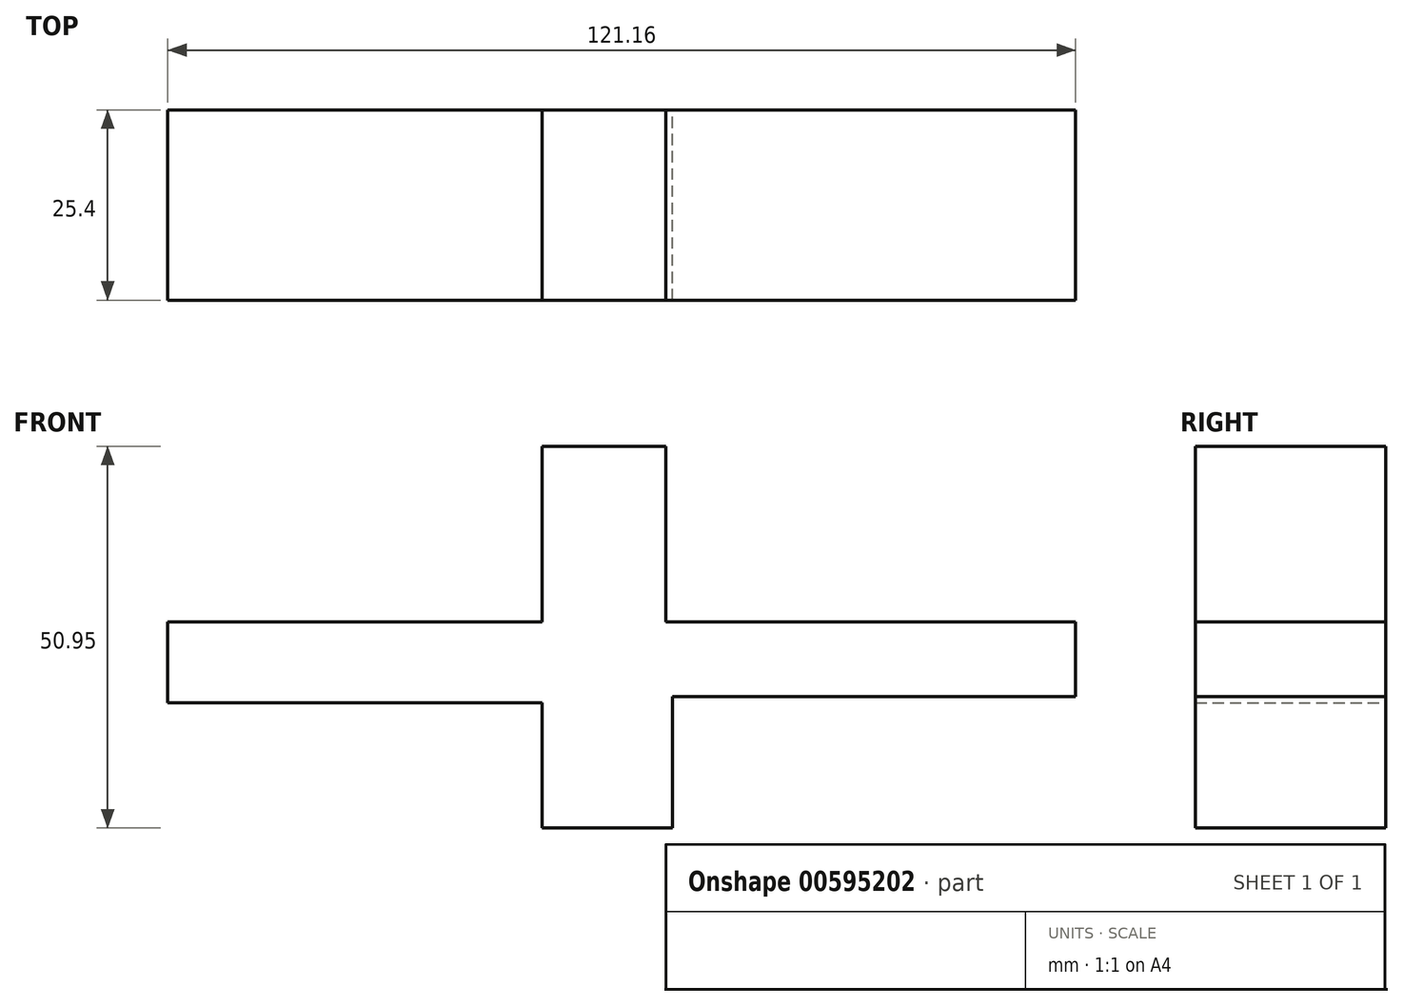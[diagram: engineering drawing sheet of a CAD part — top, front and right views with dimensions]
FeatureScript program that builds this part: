
annotation { "Feature Type Name" : "Feature", "Feature Type Description" : "" }
export const myFeature = defineFeature(function(context is Context, id is Id, definition is map)
    precondition{}
    {
        {
            var Q0;
            Q0=qCreatedBy(makeId("Front.planeOp"),FACE);
            var sketch = newSketch(context, id + "F0", { "sketchPlane" : qUnion([Q0])});
            skLineSegment(sketch, "E0", {"start": v(0, 0) * mm, "end": v(0, 23.46) * mm});
            skLineSegment(sketch, "E1", {"start": v(0, 23.46) * mm, "end": v(16.55, 23.46) * mm});
            skLineSegment(sketch, "E2", {"start": v(16.55, 23.46) * mm, "end": v(16.55, 0) * mm});
            skLineSegment(sketch, "E3", {"start": v(16.55, 0) * mm, "end": v(71.23, 0) * mm});
            skLineSegment(sketch, "E4", {"start": v(71.23, 0) * mm, "end": v(71.23, -9.93) * mm});
            skLineSegment(sketch, "E5", {"start": v(71.23, -9.93) * mm, "end": v(17.41, -9.93) * mm});
            skLineSegment(sketch, "E6", {"start": v(17.41, -9.93) * mm, "end": v(17.41, -27.49) * mm});
            skLineSegment(sketch, "E7", {"start": v(17.41, -27.49) * mm, "end": v(0, -27.49) * mm});
            skLineSegment(sketch, "E8", {"start": v(0, -27.49) * mm, "end": v(0, -10.8) * mm});
            skLineSegment(sketch, "E9", {"start": v(0, -10.8) * mm, "end": v(-49.93, -10.8) * mm});
            skLineSegment(sketch, "E10", {"start": v(-49.93, -10.8) * mm, "end": v(-49.93, 0) * mm});
            skLineSegment(sketch, "E11", {"start": v(-49.93, 0) * mm, "end": v(0, 0) * mm});
            skSolve(sketch);
        }
        {
            var Q0;
            Q0=makeQuery(id+"F0.imprint","IMPRINT",FACE,{"disambiguationData":[TD([[makeQuery(id+"F0.imprint","IMPRINT",EDGE,{"derivedFrom":sQuery(id+"F0.wireOp",EDGE,"E0")}),-1.0]])]});
            extrude(context, id + "F1", {"entities" : qUnion([Q0]), "depth" : 25.4 * mm, "offsetDistance" : 25.4 * mm});
        }
    });
